# Revit family: Haworth_ActiveComponents_ShelfExternalMounted_NEW
name_source: partatom
category: Furniture Systems
revit_build: Autodesk Revit Architecture 2015 (Build: 20141119_1515(x64)
units: mm (PartAtom-declared; Revit-internal decimal feet)

## types (8) — shared parameters
Actual Depth = 9"
Actual Height = 12"
Actual Mounting Height = 23"
Assembly Code = E2020200
Description = Haworth - Active Components Shelf - External Mounted
Drawer Height = 3"
Manufacturer = Haworth
Max. Width = 72"
Min. Width = 30"
Min/Max Widths = 30-72 in. @ 6 in. increments
Model = AZSE
Panel Thickness = 1/16"
Revision Number = 2
Shelf Height = 1/2"
Size = Verify Final Dim. w/ Haworth
Sustainability Info = https://www.haworth.com
Top Height = 2"
URL = http://www.haworth.com
URL - Product = http://www.haworth.com
Warranty = http://www.haworth.com

## per-type parameters (varying)
| type | Actual Width | Width |
| 12h 72w | 72" | 72" |
| 12h 66w | 66" | 66" |
| 12h 60w | 60" | 60" |
| 12h 54w | 54" | 54" |
| 12h 48w | 48" | 48" |
| 12h 42w | 42" | 42" |
| 12h 36w | 36" | 36" |
| 12h 30w | 30" | 30" |

## geometry (parser evidence)
native form markers: Sweep x2
no freeform markers — native parametric forms only
